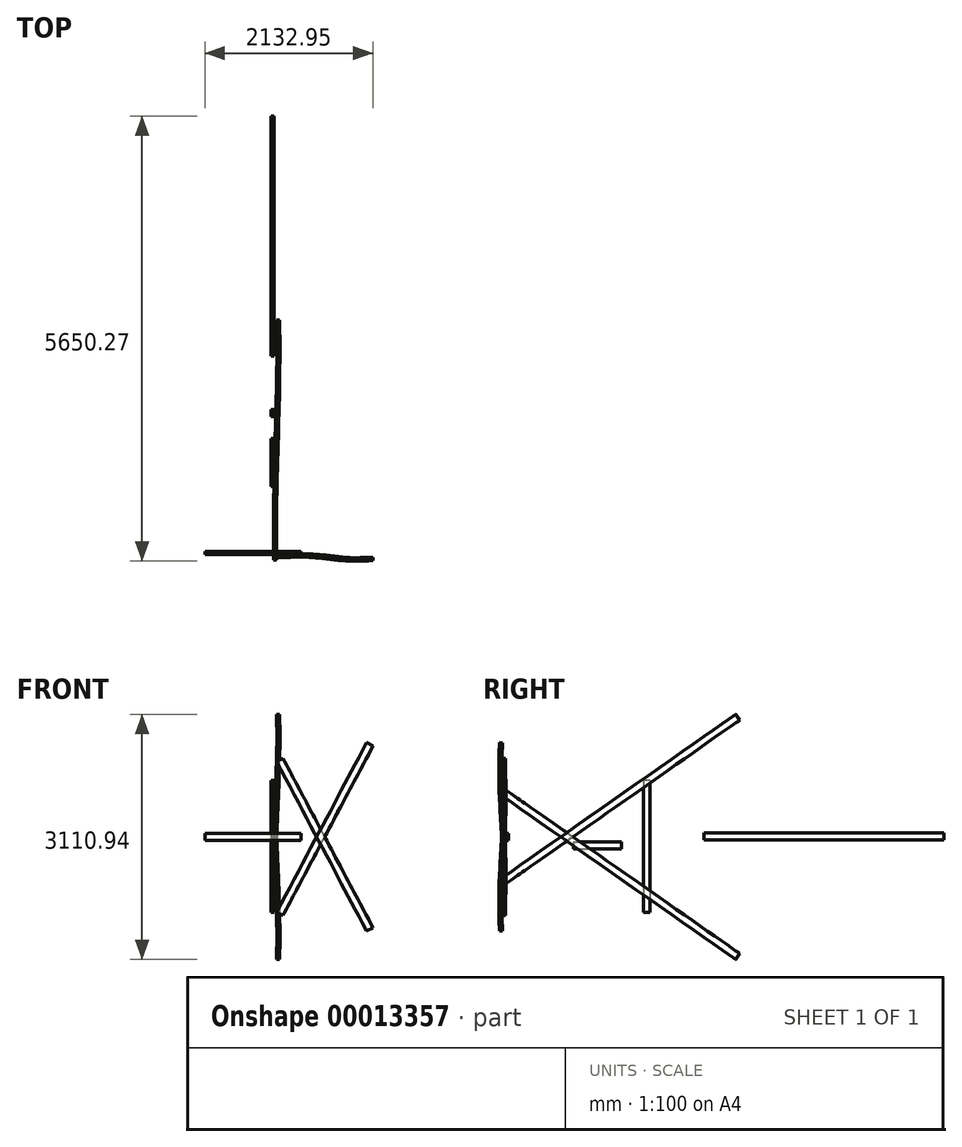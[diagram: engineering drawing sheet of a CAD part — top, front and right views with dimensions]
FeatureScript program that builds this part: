
annotation { "Feature Type Name" : "Feature", "Feature Type Description" : "" }
export const myFeature = defineFeature(function(context is Context, id is Id, definition is map)
    precondition{}
    {
        {
            var Q0;
            Q0=qCreatedBy(makeId("Right.planeOp"),FACE);
            var sketch = newSketch(context, id + "F0", { "sketchPlane" : qUnion([Q0])});
            skLineSegment(sketch, "E0", {"start": v(-58.65, 614) * mm, "end": v(2938.4, -1482.62) * mm});
            skLineSegment(sketch, "E1", {"start": v(2938.4, -1482.62) * mm, "end": v(2989.35, -1409.78) * mm});
            skLineSegment(sketch, "E2", {"start": v(2989.35, -1409.78) * mm, "end": v(-7.69, 686.84) * mm});
            skLineSegment(sketch, "E3", {"start": v(-7.69, 686.84) * mm, "end": v(-58.65, 614) * mm});
            skSolve(sketch);
        }
        {
            var Q0;
            Q0=qSketchRegion(id+"F0",true);
            extrude(context, id + "F1", {"entities" : qUnion([Q0]), "depth" : 38.1 * mm});
        }
        {
            var Q0;
            Q0=makeQuery(id+"F1.opExtrude","SWEPT_FACE",FACE,{"disambiguationData":[OSD([sQuery(id+"F0.wireOp",EDGE,"E0")])]});
            var sketch = newSketch(context, id + "F2", { "sketchPlane" : qUnion([Q0])});
            skFitSpline(sketch, "E4", {"points": [v(31.94, 400) * mm, v(31.94, -540.6) * mm, v(70.04, -2498.39) * mm, v(70.04, -3257.6) * mm], "startDerivative": vector(-16.35, -638.16) * mm, "endDerivative": vector(14.76, -413.57) * mm});
            skSolve(sketch);
        }
        {
            var Q0;
            Q0=sQuery(id+"F2.wireOp",VERTEX,"E4.start");
            var Q1;
            Q1=sQuery(id+"F2.wireOp",EDGE,"E4");
            cPlane(context, id + "F3", {"entities" : qUnion([Q0, Q1]), "cplaneType" : CPlaneType.CURVE_POINT, "offset" : 152.4 * mm, "width" : 152.4 * mm, "height" : 152.4 * mm});
        }
        {
            var Q0;
            Q0=qCreatedBy(id+"F3.planeOp",FACE);
            var sketch = newSketch(context, id + "F4", { "sketchPlane" : qUnion([Q0])});
            skLineSegment(sketch, "E5.bottom", {"start": v(-21.68, 469.49) * mm, "end": v(-59.78, 469.49) * mm});
            skLineSegment(sketch, "E5.top", {"start": v(-21.68, 380.59) * mm, "end": v(-59.78, 380.59) * mm});
            skLineSegment(sketch, "E5.left", {"start": v(-21.68, 469.49) * mm, "end": v(-21.68, 380.59) * mm});
            skLineSegment(sketch, "E5.right", {"start": v(-59.78, 469.49) * mm, "end": v(-59.78, 380.59) * mm});
            skPoint(sketch, "E6.0", {"position": v(-21.68, 469.49) * mm});
            skSolve(sketch);
        }
        {
            var Q0;
            Q0=makeQuery(id+"F4.imprint","IMPRINT",FACE,{"disambiguationData":[TD([[makeQuery(id+"F4.imprint","IMPRINT",EDGE,{"derivedFrom":sQuery(id+"F4.wireOp",EDGE,"E5.bottom")}),1.0]])]});
            var Q1;
            Q1=sQuery(id+"F2.wireOp",EDGE,"E4");
            sweep(context, id + "F5", {"profiles" : qUnion([Q0]), "path" : qUnion([Q1])});
        }
        {
            var Q0;
            Q0=makeQuery(id+"F1.opExtrude","SWEPT_BODY",BODY,{"disambiguationData":[OSD([sQuery(id+"F0.wireOp",EDGE,"E0"),sQuery(id+"F0.wireOp",EDGE,"E1"),sQuery(id+"F0.wireOp",EDGE,"E2"),sQuery(id+"F0.wireOp",EDGE,"E3")])]});
            deleteBodies(context, id + "F6", {"entities" : qUnion([Q0])});
        }
        {
            var Q0;
            Q0=makeQuery(id+"F5.opSweep","SWEPT_BODY",BODY,{"disambiguationData":[OSD([sQuery(id+"F2.wireOp",EDGE,"E4"),sQuery(id+"F4.wireOp",EDGE,"E5.bottom"),sQuery(id+"F4.wireOp",EDGE,"E5.top"),sQuery(id+"F4.wireOp",EDGE,"E5.left"),sQuery(id+"F4.wireOp",EDGE,"E5.right")])]});
            var Q1;
            Q1=qCreatedBy(makeId("Top.planeOp"),FACE);
            mirror(context, id + "F7", {"entities" : qUnion([Q0]), "mirrorPlane" : qUnion([Q1])});
        }
        {
            var Q0;
            Q0=qCreatedBy(makeId("Front.planeOp"),FACE);
            var sketch = newSketch(context, id + "F8", { "sketchPlane" : qUnion([Q0])});
            skLineSegment(sketch, "E7", {"start": v(298.65, 716.06) * mm, "end": v(1441.65, -1437.86) * mm});
            skLineSegment(sketch, "E8", {"start": v(1441.65, -1437.86) * mm, "end": v(154.45, -1437.86) * mm});
            skSolve(sketch);
        }
        {
            var Q0;
            Q0=sQuery(id+"F8.wireOp",EDGE,"E7");
            cPlane(context, id + "F9", {"entities" : qUnion([Q0]), "cplaneType" : CPlaneType.LINE_ANGLE, "offset" : 152.4 * mm, "angle" : 0 * degree, "width" : 152.4 * mm, "height" : 152.4 * mm});
        }
        {
            var Q0;
            Q0=qCreatedBy(id+"F9.planeOp",FACE);
            var sketch = newSketch(context, id + "F10", { "sketchPlane" : qUnion([Q0])});
            skFitSpline(sketch, "E9", {"points": [v(39.44, 813.37) * mm, v(39.44, -150.6) * mm, v(77.54, -924.59) * mm, v(77.54, -1625.03) * mm], "startDerivative": vector(-61.83, -2825.96) * mm, "endDerivative": vector(-56.55, -2617.11) * mm});
            skSolve(sketch);
        }
        {
            var Q0;
            Q0=sQuery(id+"F10.wireOp",EDGE,"E9");
            var Q1;
            Q1=sQuery(id+"F10.wireOp",VERTEX,"E9.start");
            cPlane(context, id + "F11", {"entities" : qUnion([Q0, Q1]), "cplaneType" : CPlaneType.CURVE_POINT, "offset" : 152.4 * mm, "width" : 152.4 * mm, "height" : 152.4 * mm});
        }
        {
            var Q0;
            Q0=qCreatedBy(id+"F11.planeOp",FACE);
            var sketch = newSketch(context, id + "F12", { "sketchPlane" : qUnion([Q0])});
            skLineSegment(sketch, "E10.bottom", {"start": v(510.77, 52.78) * mm, "end": v(599.67, 52.78) * mm});
            skLineSegment(sketch, "E10.top", {"start": v(510.77, 14.68) * mm, "end": v(599.67, 14.68) * mm});
            skLineSegment(sketch, "E10.left", {"start": v(510.77, 52.78) * mm, "end": v(510.77, 14.68) * mm});
            skLineSegment(sketch, "E10.right", {"start": v(599.67, 52.78) * mm, "end": v(599.67, 14.68) * mm});
            skSolve(sketch);
        }
        {
            var Q0;
            Q0=makeQuery(id+"F12.imprint","IMPRINT",FACE,{"disambiguationData":[TD([[makeQuery(id+"F12.imprint","IMPRINT",EDGE,{"derivedFrom":sQuery(id+"F12.wireOp",EDGE,"E10.bottom")}),-1.0]])]});
            var Q1;
            Q1=sQuery(id+"F10.wireOp",EDGE,"E9");
            sweep(context, id + "F13", {"profiles" : qUnion([Q0]), "path" : qUnion([Q1])});
        }
        {
            var Q0;
            Q0=makeQuery(id+"F13.opSweep","SWEPT_BODY",BODY,{"disambiguationData":[OSD([sQuery(id+"F10.wireOp",EDGE,"E9"),sQuery(id+"F12.wireOp",EDGE,"E10.bottom"),sQuery(id+"F12.wireOp",EDGE,"E10.top"),sQuery(id+"F12.wireOp",EDGE,"E10.left"),sQuery(id+"F12.wireOp",EDGE,"E10.right")])]});
            var Q1;
            Q1=qCreatedBy(makeId("Top.planeOp"),FACE);
            mirror(context, id + "F14", {"entities" : qUnion([Q0]), "mirrorPlane" : qUnion([Q1])});
        }
        {
            var Q0;
            Q0=qCreatedBy(makeId("Right.planeOp"),FACE);
            var sketch = newSketch(context, id + "F15", { "sketchPlane" : qUnion([Q0])});
            skLineSegment(sketch, "E11.bottom", {"start": v(2481.35, 52.5) * mm, "end": v(5529.35, 52.5) * mm});
            skLineSegment(sketch, "E11.top", {"start": v(2481.35, -36.4) * mm, "end": v(5529.35, -36.4) * mm});
            skLineSegment(sketch, "E11.left", {"start": v(2481.35, 52.5) * mm, "end": v(2481.35, -36.4) * mm});
            skLineSegment(sketch, "E11.right", {"start": v(5529.35, 52.5) * mm, "end": v(5529.35, -36.4) * mm});
            skSolve(sketch);
        }
        {
            var Q0;
            Q0=qSketchRegion(id+"F15",true);
            extrude(context, id + "F16", {"entities" : qUnion([Q0]), "depth" : 38.1 * mm});
        }
        {
            var Q0;
            Q0=qCreatedBy(makeId("Front.planeOp"),FACE);
            var sketch = newSketch(context, id + "F17", { "sketchPlane" : qUnion([Q0])});
            skLineSegment(sketch, "E12.bottom", {"start": v(377.5, 41.64) * mm, "end": v(-841.7, 41.64) * mm});
            skLineSegment(sketch, "E12.top", {"start": v(377.5, -47.26) * mm, "end": v(-841.7, -47.26) * mm});
            skLineSegment(sketch, "E12.left", {"start": v(377.5, 41.64) * mm, "end": v(377.5, -47.26) * mm});
            skLineSegment(sketch, "E12.right", {"start": v(-841.7, 41.64) * mm, "end": v(-841.7, -47.26) * mm});
            skSolve(sketch);
        }
        {
            var Q0;
            Q0=qSketchRegion(id+"F17",true);
            extrude(context, id + "F18", {"entities" : qUnion([Q0]), "depth" : 38.1 * mm});
        }
        {
            var Q0;
            Q0=qCreatedBy(makeId("Right.planeOp"),FACE);
            var sketch = newSketch(context, id + "F19", { "sketchPlane" : qUnion([Q0])});
            skLineSegment(sketch, "E13.bottom", {"start": v(824.82, -61.77) * mm, "end": v(1434.42, -61.77) * mm});
            skLineSegment(sketch, "E13.top", {"start": v(824.82, -150.67) * mm, "end": v(1434.42, -150.67) * mm});
            skLineSegment(sketch, "E13.left", {"start": v(824.82, -61.77) * mm, "end": v(824.82, -150.67) * mm});
            skLineSegment(sketch, "E13.right", {"start": v(1434.42, -61.77) * mm, "end": v(1434.42, -150.67) * mm});
            skSolve(sketch);
        }
        {
            var Q0;
            Q0=qSketchRegion(id+"F19",true);
            extrude(context, id + "F20", {"entities" : qUnion([Q0]), "depth" : 38.1 * mm});
        }
        {
            var Q0;
            Q0=qCreatedBy(makeId("Right.planeOp"),FACE);
            var sketch = newSketch(context, id + "F21", { "sketchPlane" : qUnion([Q0])});
            skLineSegment(sketch, "E14.bottom", {"start": v(1801.6, 718.38) * mm, "end": v(1712.7, 718.38) * mm});
            skLineSegment(sketch, "E14.top", {"start": v(1801.6, -958.02) * mm, "end": v(1712.7, -958.02) * mm});
            skLineSegment(sketch, "E14.left", {"start": v(1801.6, 718.38) * mm, "end": v(1801.6, -958.02) * mm});
            skLineSegment(sketch, "E14.right", {"start": v(1712.7, 718.38) * mm, "end": v(1712.7, -958.02) * mm});
            skSolve(sketch);
        }
        {
            var Q0;
            Q0=qSketchRegion(id+"F21",true);
            extrude(context, id + "F22", {"entities" : qUnion([Q0]), "depth" : 38.1 * mm});
        }
    });
